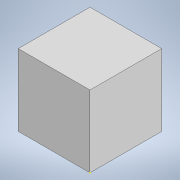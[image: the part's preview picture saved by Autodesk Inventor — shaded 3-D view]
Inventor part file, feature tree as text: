
AUTODESK INVENTOR PART (.ipt)
format: ipt  version: 2021 (Build 250183000, 183)  size: 113,664 bytes
history: native  units: in
note: dims shown in document units (in); Inventor stores cm internally (conversion verified against a paired STEP export)
features: sketch x3, extrude x2
ambient origin geometry x8: Origin, YZ Plane, XZ Plane, XY Plane, X Axis, Y Axis, Z Axis, Center Point
bodies: Solid1 (feature_tree)
feature tree (5):
  sketch  "Sketch1"  dims[d1=0.6299in d2=0.6299in]
  extrude  "Extrusion1"  Depth=0.6299in
  extrude  "Extrusion2"  Depth=0.5118in TaperAngle=0.0deg
  sketch  "Sketch2"  dims[d8=0.6299in d9=0.0in d18=0.5118in d19=0.0in]
  sketch  "Sketch3"  dims[d28=0.0709in d31=0.0709in d32=0.5118in d33=0.1417in d34=0.0709in d35=0.0709in d37=0.0709in d38=0.5118in d42=0.1417in d43=0.5118in]
